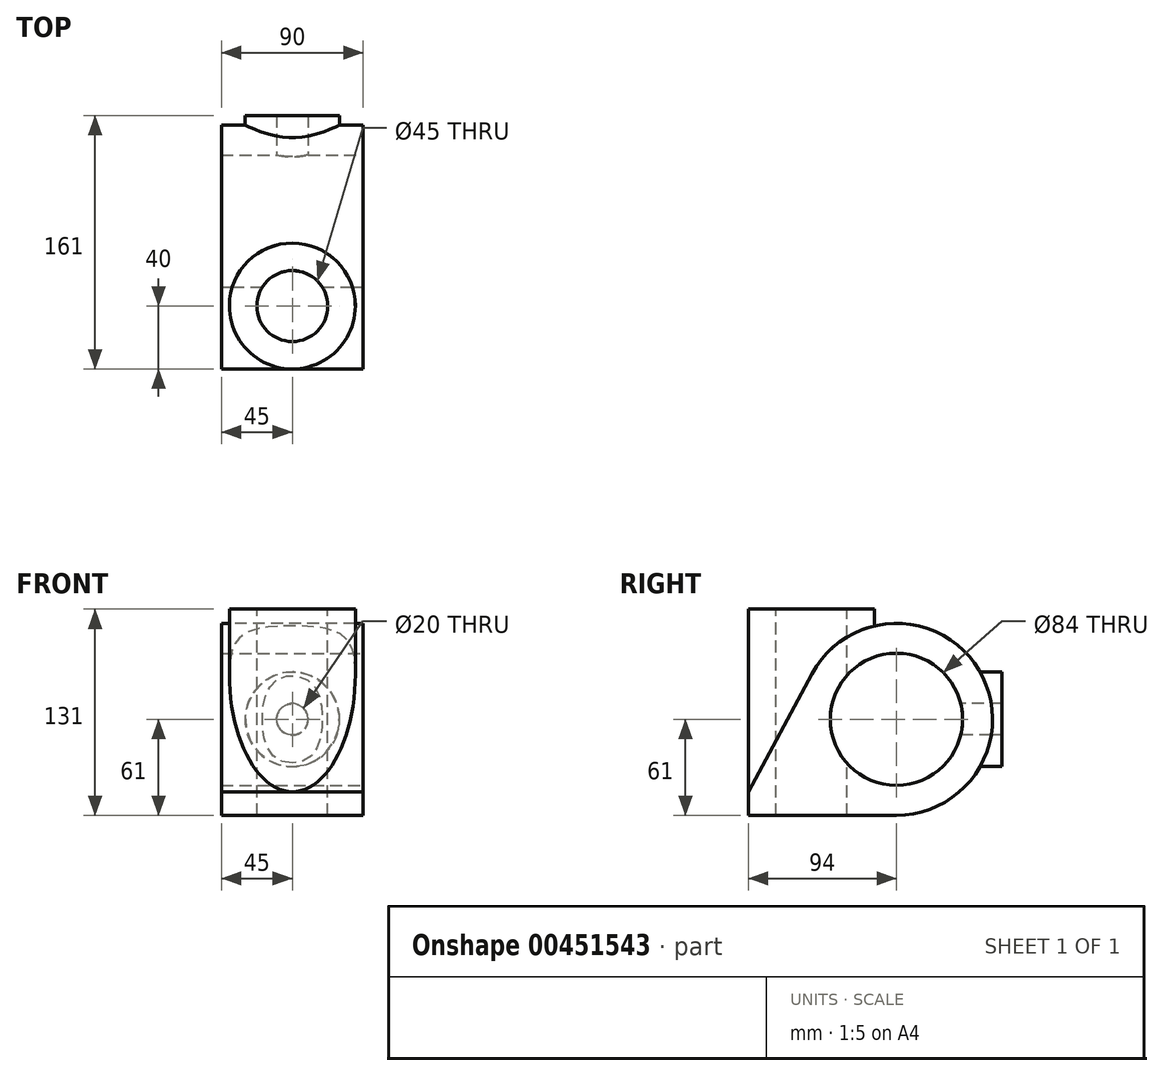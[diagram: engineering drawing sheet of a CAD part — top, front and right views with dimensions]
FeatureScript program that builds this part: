
annotation { "Feature Type Name" : "Feature", "Feature Type Description" : "" }
export const myFeature = defineFeature(function(context is Context, id is Id, definition is map)
    precondition{}
    {
        {
            var Q0;
            Q0=qCreatedBy(makeId("Right.planeOp"),FACE);
            var sketch = newSketch(context, id + "F0", { "sketchPlane" : qUnion([Q0])});
            skLineSegment(sketch, "E0", {"start": v(-94, -46) * mm, "end": v(-53.72, 28.9) * mm});
            skArc(sketch, "E1", {"start": v(0, -61) * mm, "mid": v(52.36, 31.3) * mm, "end": v(-53.72, 28.9) * mm});
            skLineSegment(sketch, "E2", {"start": v(-94, -46) * mm, "end": v(-94, -61) * mm});
            skLineSegment(sketch, "E3", {"start": v(-94, -61) * mm, "end": v(0, -61) * mm});
            skSolve(sketch);
        }
        {
            var Q0;
            Q0 = qSketchRegion(id + "F0", true);
            extrude(context, id + "F1", {"entities" : qUnion([Q0]), "depth" : 90 * mm, "symmetric" : true});
        }
        {
            var Q0;
            Q0=qCreatedBy(makeId("Top.planeOp"),FACE);
            var sketch = newSketch(context, id + "F2", { "sketchPlane" : qUnion([Q0])});
            skCircle(sketch, "E4", {"center": v(0, -54) * mm, "radius": 40 * mm});
            skSolve(sketch);
        }
        {
            var Q0;
            Q0 = qSketchRegion(id + "F2", true);
            var Q1;
            Q1=makeQuery(id+"F1.opExtrude","SWEPT_FACE",FACE,{"disambiguationData":[OSD([sQuery(id+"F0.wireOp",EDGE,"E3")])]});
            extrude(context, id + "F3", {"entities" : qUnion([Q0]), "operationType" : NewBodyOperationType.ADD, "depth" : 70 * mm, "hasSecondDirection" : true, "secondDirectionBound" : BoundingType.UP_TO_SURFACE, "secondDirectionOppositeDirection" : true, "secondDirectionBoundEntityFace" : qUnion([Q1]), "secondDirectionDepth" : 25 * mm});
        }
        {
            var Q0;
            Q0=qCreatedBy(makeId("Front.planeOp"),FACE);
            var sketch = newSketch(context, id + "F4", { "sketchPlane" : qUnion([Q0])});
            skCircle(sketch, "E5", {"center": v(0, 0) * mm, "radius": 30 * mm});
            skSolve(sketch);
        }
        {
            var Q0;
            Q0 = qSketchRegion(id + "F4", true);
            extrude(context, id + "F5", {"entities" : qUnion([Q0]), "operationType" : NewBodyOperationType.ADD, "oppositeDirection" : true, "depth" : 67 * mm});
        }
        {
            var Q0;
            Q0=makeQuery(id+"F3.opExtrude","CAP_FACE",FACE,{"disambiguationData":[OSD([sQuery(id+"F2.wireOp",EDGE,"E4")])],"isStart":false});
            var sketch = newSketch(context, id + "F6", { "sketchPlane" : qUnion([Q0])});
            skCircle(sketch, "E6", {"center": v(0, -54) * mm, "radius": 22.5 * mm});
            skSolve(sketch);
        }
        {
            var Q0;
            Q0=qCreatedBy(makeId("Right.planeOp"),FACE);
            var sketch = newSketch(context, id + "F7", { "sketchPlane" : qUnion([Q0])});
            skCircle(sketch, "E7", {"center": v(0, 0) * mm, "radius": 42 * mm});
            skSolve(sketch);
        }
        {
            var Q0;
            Q0=qCreatedBy(makeId("Front.planeOp"),FACE);
            var sketch = newSketch(context, id + "F8", { "sketchPlane" : qUnion([Q0])});
            skCircle(sketch, "E8", {"center": v(0, 0) * mm, "radius": 10 * mm});
            skSolve(sketch);
        }
        {
            var Q0;
            Q0 = qSketchRegion(id + "F6", true);
            extrude(context, id + "F9", {"entities" : qUnion([Q0]), "operationType" : NewBodyOperationType.REMOVE, "endBound" : BoundingType.THROUGH_ALL, "oppositeDirection" : true, "depth" : 25 * mm});
        }
        {
            var Q0;
            Q0 = qSketchRegion(id + "F7", true);
            var Q1;
            Q1=makeQuery(id+"F1.opExtrude","CAP_FACE",FACE,{"disambiguationData":[OSD([sQuery(id+"F0.wireOp",EDGE,"E0"),sQuery(id+"F0.wireOp",EDGE,"E1"),sQuery(id+"F0.wireOp",EDGE,"E2"),sQuery(id+"F0.wireOp",EDGE,"E3")])],"isStart":false});
            var Q2;
            Q2=makeQuery(id+"F1.opExtrude","CAP_FACE",FACE,{"disambiguationData":[OSD([sQuery(id+"F0.wireOp",EDGE,"E0"),sQuery(id+"F0.wireOp",EDGE,"E1"),sQuery(id+"F0.wireOp",EDGE,"E2"),sQuery(id+"F0.wireOp",EDGE,"E3")])],"isStart":true});
            extrude(context, id + "F10", {"entities" : qUnion([Q0]), "operationType" : NewBodyOperationType.REMOVE, "endBound" : BoundingType.UP_TO_NEXT, "oppositeDirection" : true, "endBoundEntityFace" : qUnion([Q1]), "depth" : 132 * mm, "hasSecondDirection" : true, "secondDirectionBound" : BoundingType.UP_TO_NEXT, "secondDirectionOppositeDirection" : false, "secondDirectionBoundEntityFace" : qUnion([Q2]), "secondDirectionDepth" : 25 * mm});
        }
        {
            var Q0;
            Q0 = qSketchRegion(id + "F8", true);
            extrude(context, id + "F11", {"entities" : qUnion([Q0]), "operationType" : NewBodyOperationType.REMOVE, "endBound" : BoundingType.THROUGH_ALL, "oppositeDirection" : true, "depth" : 25 * mm});
        }
    });
